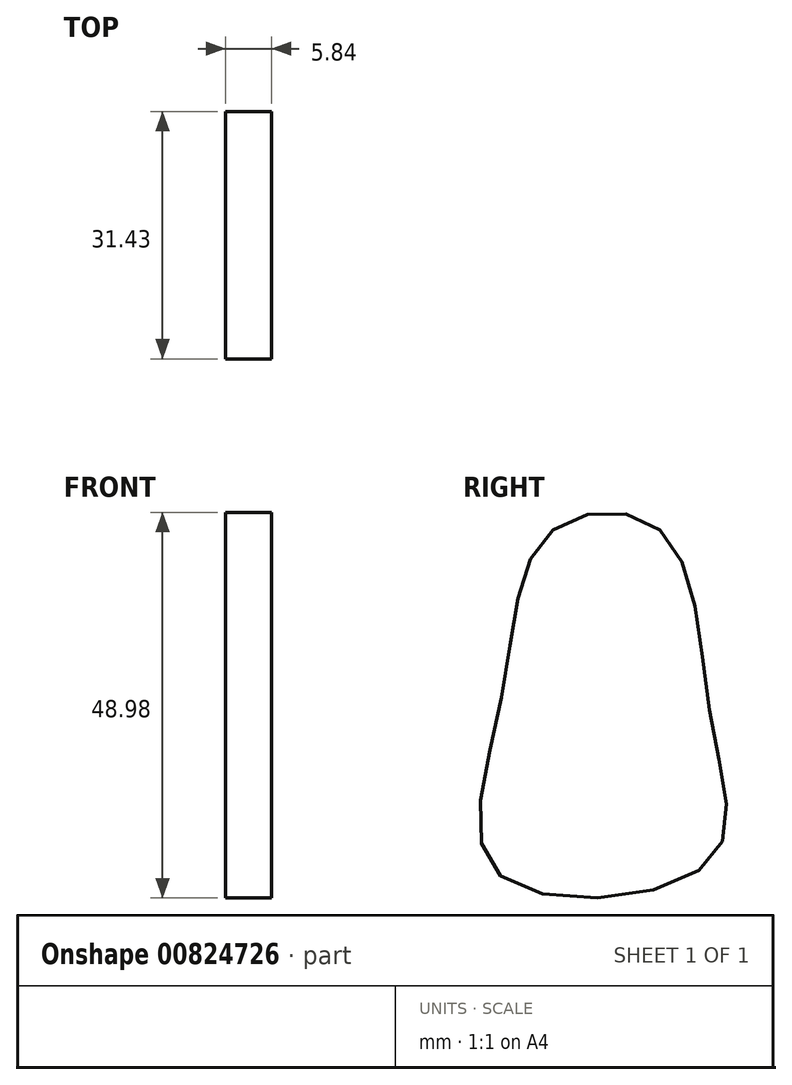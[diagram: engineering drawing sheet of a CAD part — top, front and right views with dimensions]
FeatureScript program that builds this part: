
annotation { "Feature Type Name" : "Feature", "Feature Type Description" : "" }
export const myFeature = defineFeature(function(context is Context, id is Id, definition is map)
    precondition{}
    {
        {
            var Q0;
            Q0=qCreatedBy(makeId("Right.planeOp"),FACE);
            var sketch = newSketch(context, id + "F0", { "sketchPlane" : qUnion([Q0])});
            skFitSpline(sketch, "E0", {"points": [v(-43.63, 28.86) * mm, v(-37.45, 49.8) * mm, v(-23.5, 50.07) * mm, v(-17.05, 26.18) * mm, v(-17.59, 7.65) * mm, v(-43.9, 6.3) * mm, v(-43.63, 28.86) * mm]});
            skSolve(sketch);
        }
        {
            var Q0;
            Q0=makeQuery(id+"F0.imprint","IMPRINT",FACE,{"disambiguationData":[TD([[makeQuery(id+"F0.imprint","IMPRINT",EDGE,{"derivedFrom":sQuery(id+"F0.wireOp",EDGE,"E0")}),-1.0]])]});
            extrude(context, id + "F1", {"entities" : qUnion([Q0]), "depth" : 5.84 * mm, "offsetDistance" : 25.4 * mm});
        }
    });
